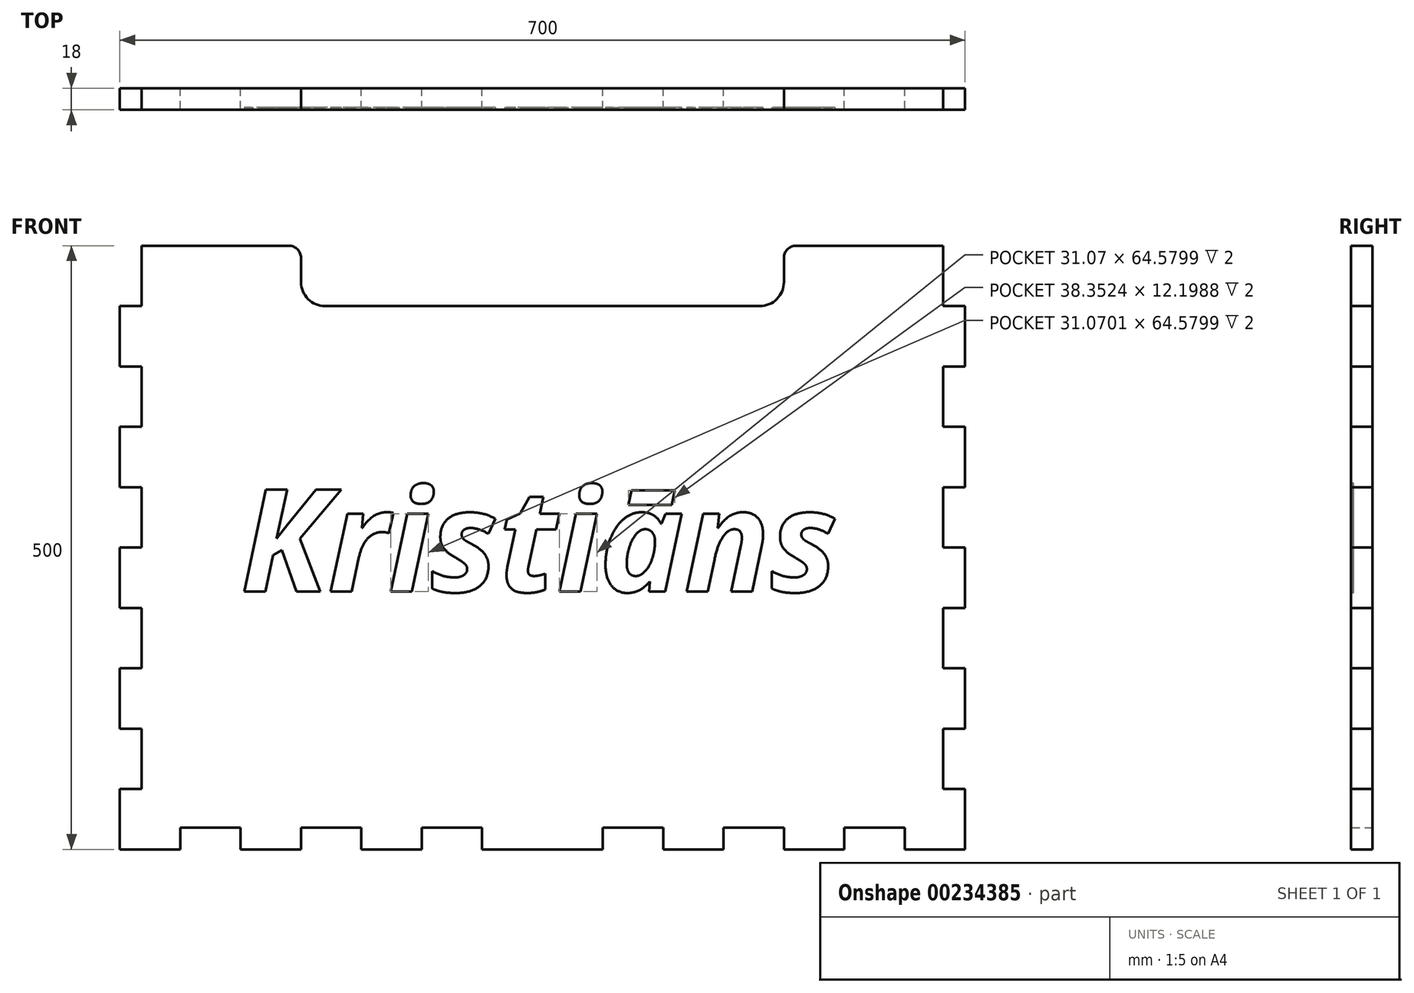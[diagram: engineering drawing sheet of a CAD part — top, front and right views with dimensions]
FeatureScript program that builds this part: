
annotation { "Feature Type Name" : "Feature", "Feature Type Description" : "" }
export const myFeature = defineFeature(function(context is Context, id is Id, definition is map)
    precondition{}
    {
        {
            var Q0;
            Q0=qCreatedBy(makeId("Front.planeOp"),FACE);
            var sketch = newSketch(context, id + "F0", { "sketchPlane" : qUnion([Q0])});
            skLineSegment(sketch, "E0.bottom", {"start": v(-332, 250) * mm, "end": v(-210, 250) * mm});
            skLineSegment(sketch, "E0.left", {"start": v(-350, 200) * mm, "end": v(-350, 150) * mm});
            skLineSegment(sketch, "E0.right", {"start": v(350, 200) * mm, "end": v(350, 150) * mm});
            skPoint(sketch, "E0.middle", {"position": v(0, 0) * mm});
            skLineSegment(sketch, "E1.top", {"start": v(-180, 200) * mm, "end": v(180, 200) * mm});
            skLineSegment(sketch, "E1.left", {"start": v(-200, 240) * mm, "end": v(-200, 220) * mm});
            skLineSegment(sketch, "E1.right", {"start": v(200, 240) * mm, "end": v(200, 220) * mm});
            skPoint(sketch, "E1.middle", {"position": v(0, 225) * mm});
            skPoint(sketch, "E2.visualSharp", {"position": v(-200, 200) * mm});
            skArc(sketch, "E2.filletArc", {"start": v(-200, 220) * mm, "mid": v(-194.14, 205.86) * mm, "end": v(-180, 200) * mm});
            skPoint(sketch, "E3.visualSharp", {"position": v(200, 200) * mm});
            skArc(sketch, "E3.filletArc", {"start": v(180, 200) * mm, "mid": v(194.14, 205.86) * mm, "end": v(200, 220) * mm});
            skLineSegment(sketch, "E4.trimOffspring", {"start": v(210, 250) * mm, "end": v(332, 250) * mm});
            skPoint(sketch, "E5.visualSharp", {"position": v(-200, 250) * mm});
            skArc(sketch, "E5.filletArc", {"start": v(-200, 240) * mm, "mid": v(-202.93, 247.07) * mm, "end": v(-210, 250) * mm});
            skPoint(sketch, "E6.visualSharp", {"position": v(200, 250) * mm});
            skArc(sketch, "E6.filletArc", {"start": v(210, 250) * mm, "mid": v(202.93, 247.07) * mm, "end": v(200, 240) * mm});
            skLineSegment(sketch, "E7.top", {"start": v(-350, 150) * mm, "end": v(-332, 150) * mm});
            skLineSegment(sketch, "E8.top", {"start": v(-350, 100) * mm, "end": v(-332, 100) * mm});
            skLineSegment(sketch, "E8.right", {"start": v(-332, 150) * mm, "end": v(-332, 100) * mm});
            skLineSegment(sketch, "E9.top", {"start": v(-350, 50) * mm, "end": v(-332, 50) * mm});
            skLineSegment(sketch, "E9.left", {"start": v(-350, 100) * mm, "end": v(-350, 50) * mm});
            skLineSegment(sketch, "E10.top", {"start": v(-350, 0) * mm, "end": v(-332, 0) * mm});
            skLineSegment(sketch, "E10.right", {"start": v(-332, 50) * mm, "end": v(-332, 0) * mm});
            skLineSegment(sketch, "E11.top", {"start": v(-350, -50) * mm, "end": v(-332, -50) * mm});
            skLineSegment(sketch, "E11.left", {"start": v(-350, 0) * mm, "end": v(-350, -50) * mm});
            skLineSegment(sketch, "E12.top", {"start": v(-350, -100) * mm, "end": v(-332, -100) * mm});
            skLineSegment(sketch, "E12.right", {"start": v(-332, -50) * mm, "end": v(-332, -100) * mm});
            skLineSegment(sketch, "E13.top", {"start": v(-350, -150) * mm, "end": v(-332, -150) * mm});
            skLineSegment(sketch, "E13.left", {"start": v(-350, -100) * mm, "end": v(-350, -150) * mm});
            skPoint(sketch, "E14.orphan", {"position": v(-350, -250) * mm});
            skLineSegment(sketch, "E15.top", {"start": v(350, 200) * mm, "end": v(332, 200) * mm});
            skLineSegment(sketch, "E15.right", {"start": v(332, 250) * mm, "end": v(332, 200) * mm});
            skLineSegment(sketch, "E16.bottom", {"start": v(332, 200) * mm, "end": v(350, 200) * mm});
            skLineSegment(sketch, "E16.top", {"start": v(332, 150) * mm, "end": v(350, 150) * mm});
            skLineSegment(sketch, "E17.top", {"start": v(332, 100) * mm, "end": v(350, 100) * mm});
            skLineSegment(sketch, "E17.left", {"start": v(332, 150) * mm, "end": v(332, 100) * mm});
            skLineSegment(sketch, "E18.top", {"start": v(332, 50) * mm, "end": v(350, 50) * mm});
            skLineSegment(sketch, "E18.right", {"start": v(350, 100) * mm, "end": v(350, 50) * mm});
            skLineSegment(sketch, "E19.top", {"start": v(332, 0) * mm, "end": v(350, 0) * mm});
            skLineSegment(sketch, "E19.left", {"start": v(332, 50) * mm, "end": v(332, 0) * mm});
            skLineSegment(sketch, "E20.top", {"start": v(332, -50) * mm, "end": v(350, -50) * mm});
            skLineSegment(sketch, "E20.right", {"start": v(350, 0) * mm, "end": v(350, -50) * mm});
            skLineSegment(sketch, "E21.top", {"start": v(332, -100) * mm, "end": v(350, -100) * mm});
            skLineSegment(sketch, "E21.left", {"start": v(332, -50) * mm, "end": v(332, -100) * mm});
            skLineSegment(sketch, "E22.top", {"start": v(332, -150) * mm, "end": v(350, -150) * mm});
            skLineSegment(sketch, "E22.right", {"start": v(350, -100) * mm, "end": v(350, -150) * mm});
            skLineSegment(sketch, "E23.top", {"start": v(332, -200) * mm, "end": v(350, -200) * mm});
            skLineSegment(sketch, "E23.left", {"start": v(332, -150) * mm, "end": v(332, -200) * mm});
            skLineSegment(sketch, "E24.right", {"start": v(350, -200) * mm, "end": v(350, -250) * mm});
            skPoint(sketch, "E15.bottom.start.orphan", {"position": v(350, 250) * mm});
            skLineSegment(sketch, "E25.right", {"start": v(-300, -250) * mm, "end": v(-300, -232) * mm});
            skLineSegment(sketch, "E26.left", {"start": v(-300, -232) * mm, "end": v(-300, -250) * mm});
            skLineSegment(sketch, "E26.right", {"start": v(-250, -232) * mm, "end": v(-250, -250) * mm});
            skLineSegment(sketch, "E27.right", {"start": v(-200, -232) * mm, "end": v(-200, -250) * mm});
            skLineSegment(sketch, "E28.right", {"start": v(-150, -232) * mm, "end": v(-150, -250) * mm});
            skLineSegment(sketch, "E29.right", {"start": v(-100, -232) * mm, "end": v(-100, -250) * mm});
            skLineSegment(sketch, "E30.right", {"start": v(-50, -232) * mm, "end": v(-50, -250) * mm});
            skLineSegment(sketch, "E31.right", {"start": v(50, -232) * mm, "end": v(50, -250) * mm});
            skLineSegment(sketch, "E32.bottom", {"start": v(50, -232) * mm, "end": v(100, -232) * mm});
            skLineSegment(sketch, "E32.right", {"start": v(100, -232) * mm, "end": v(100, -250) * mm});
            skLineSegment(sketch, "E33.right", {"start": v(150, -232) * mm, "end": v(150, -250) * mm});
            skLineSegment(sketch, "E34.bottom", {"start": v(150, -232) * mm, "end": v(200, -232) * mm});
            skLineSegment(sketch, "E34.right", {"start": v(200, -232) * mm, "end": v(200, -250) * mm});
            skLineSegment(sketch, "E35.top", {"start": v(200, -250) * mm, "end": v(250, -250) * mm});
            skLineSegment(sketch, "E35.right", {"start": v(250, -232) * mm, "end": v(250, -250) * mm});
            skLineSegment(sketch, "E36.bottom", {"start": v(250, -232) * mm, "end": v(300, -232) * mm});
            skLineSegment(sketch, "E36.right", {"start": v(300, -232) * mm, "end": v(300, -250) * mm});
            skLineSegment(sketch, "E37.top", {"start": v(300, -250) * mm, "end": v(350, -250) * mm});
            skLineSegment(sketch, "E37.right", {"start": v(350, -232) * mm, "end": v(350, -250) * mm});
            skPoint(sketch, "E38.orphan", {"position": v(-332, -250) * mm});
            skLineSegment(sketch, "E39.right", {"start": v(-350, -232) * mm, "end": v(-350, -200) * mm});
            skPoint(sketch, "E40.top.end.orphan", {"position": v(-332, -200) * mm});
            skLineSegment(sketch, "E41.left", {"start": v(-332, -182) * mm, "end": v(-332, -150) * mm});
            skLineSegment(sketch, "E42.trimOffspring", {"start": v(-350, -150) * mm, "end": v(-350, -100) * mm});
            skLineSegment(sketch, "E43.trimOffspring", {"start": v(-332, -100) * mm, "end": v(-332, -50) * mm});
            skLineSegment(sketch, "E44.trimOffspring", {"start": v(-350, -50) * mm, "end": v(-350, 0) * mm});
            skLineSegment(sketch, "E45.trimOffspring", {"start": v(-332, 0) * mm, "end": v(-332, 50) * mm});
            skLineSegment(sketch, "E46.trimOffspring", {"start": v(-350, 50) * mm, "end": v(-350, 100) * mm});
            skLineSegment(sketch, "E47.trimOffspring", {"start": v(-332, 100) * mm, "end": v(-332, 150) * mm});
            skLineSegment(sketch, "E48.trimOffspring", {"start": v(-350, 150) * mm, "end": v(-350, 200) * mm});
            skLineSegment(sketch, "E49.bottom", {"start": v(-332, 150) * mm, "end": v(-350, 150) * mm});
            skPoint(sketch, "E49.right.end.orphan", {"position": v(-350, 200) * mm});
            skLineSegment(sketch, "E50.top", {"start": v(-350, 200) * mm, "end": v(-332, 200) * mm});
            skLineSegment(sketch, "E51.bottom", {"start": v(-332, 200) * mm, "end": v(-350, 200) * mm});
            skLineSegment(sketch, "E51.left", {"start": v(-332, 200) * mm, "end": v(-332, 250) * mm});
            skLineSegment(sketch, "E52.bottom", {"start": v(-332, -200) * mm, "end": v(-350, -200) * mm});
            skLineSegment(sketch, "E52.left", {"start": v(-332, -200) * mm, "end": v(-332, -150) * mm});
            skLineSegment(sketch, "E53.trimOffspring", {"start": v(-332, 100) * mm, "end": v(-332, 250) * mm});
            skPoint(sketch, "E52.top.end.orphan", {"position": v(-350, 250) * mm});
            skLineSegment(sketch, "E54.bottom", {"start": v(-350, -200) * mm, "end": v(-332, -200) * mm});
            skLineSegment(sketch, "E54.top", {"start": v(-350, -250) * mm, "end": v(-300, -250) * mm});
            skLineSegment(sketch, "E54.left", {"start": v(-350, -200) * mm, "end": v(-350, -250) * mm});
            skLineSegment(sketch, "E55.left", {"start": v(-350, -232) * mm, "end": v(-350, -250) * mm});
            skLineSegment(sketch, "E56.trimOffspring", {"start": v(-300, -232) * mm, "end": v(-250, -232) * mm});
            skLineSegment(sketch, "E57.trimOffspring", {"start": v(-250, -250) * mm, "end": v(-200, -250) * mm});
            skLineSegment(sketch, "E58.trimOffspring", {"start": v(-150, -250) * mm, "end": v(-100, -250) * mm});
            skLineSegment(sketch, "E59.trimOffspring", {"start": v(-50, -250) * mm, "end": v(0, -250) * mm});
            skLineSegment(sketch, "E60", {"start": v(100, -250) * mm, "end": v(150, -250) * mm});
            skLineSegment(sketch, "E61", {"start": v(0, -250) * mm, "end": v(50, -250) * mm});
            skLineSegment(sketch, "E62.trimOffspring", {"start": v(-200, -232) * mm, "end": v(-150, -232) * mm});
            skLineSegment(sketch, "E63.trimOffspring", {"start": v(-100, -232) * mm, "end": v(-50, -232) * mm});
            skSolve(sketch);
        }
        {
            var Q0;
            Q0 = qSketchRegion(id + "F0", true);
            extrude(context, id + "F1", {"entities" : qUnion([Q0]), "depth" : 18 * mm});
        }
        {
            var Q0;
            Q0=makeQuery(id+"F1.opExtrude","CAP_FACE",FACE,{"disambiguationData":[OSD([sQuery(id+"F0.wireOp",EDGE,"E0.bottom"),sQuery(id+"F0.wireOp",EDGE,"E0.top"),sQuery(id+"F0.wireOp",EDGE,"E0.left"),sQuery(id+"F0.wireOp",EDGE,"E0.right"),sQuery(id+"F0.wireOp",EDGE,"E1.top"),sQuery(id+"F0.wireOp",EDGE,"E1.left"),sQuery(id+"F0.wireOp",EDGE,"E1.right"),sQuery(id+"F0.wireOp",EDGE,"E2.filletArc"),sQuery(id+"F0.wireOp",EDGE,"E3.filletArc"),sQuery(id+"F0.wireOp",EDGE,"E4.trimOffspring"),sQuery(id+"F0.wireOp",EDGE,"E5.filletArc"),sQuery(id+"F0.wireOp",EDGE,"E6.filletArc")])],"isStart":false});
            var sketch = newSketch(context, id + "F2", { "sketchPlane" : qUnion([Q0])});
            skText(sketch, "E64", { "text": "Kristiāns", "fontName": "OpenSans-BoldItalic.ttf"});
            const initialGuessF2  = {"E64": [-0.25, -0.0365, 1, 0, 0.08517]};
            skSetInitialGuess(sketch, initialGuessF2);
            skSolve(sketch);
        }
        {
            var Q0;
            Q0 = qSketchRegion(id + "F2", true);
            extrude(context, id + "F3", {"entities" : qUnion([Q0]), "operationType" : NewBodyOperationType.REMOVE, "oppositeDirection" : true, "depth" : 2 * mm});
        }
    });
